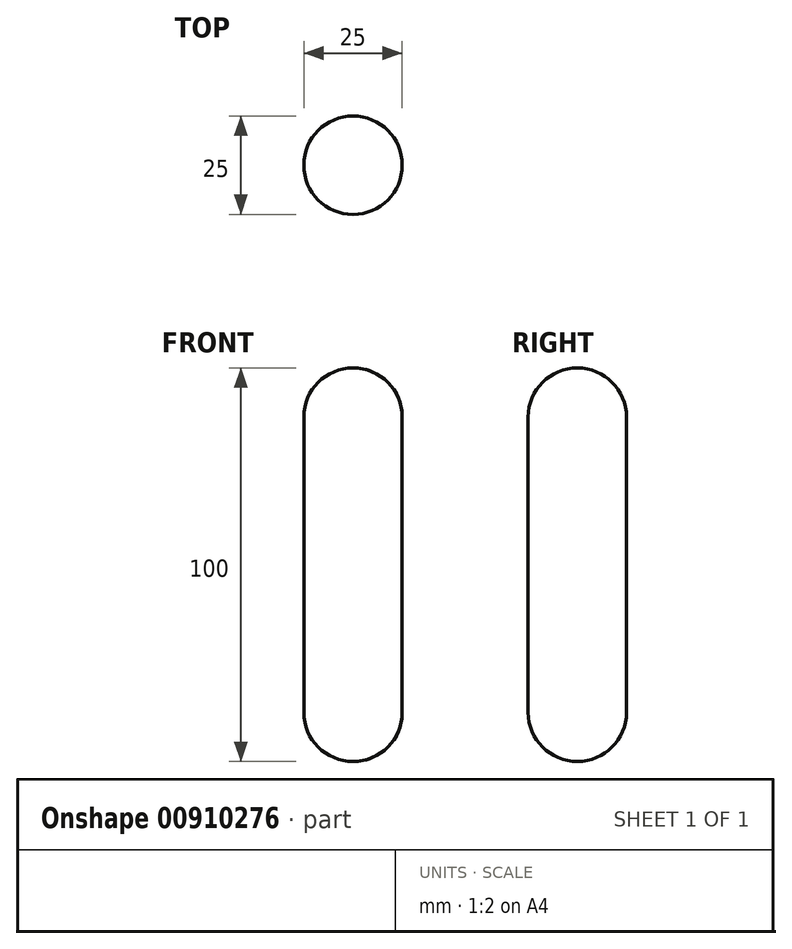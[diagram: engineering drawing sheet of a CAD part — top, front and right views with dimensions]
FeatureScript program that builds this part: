
annotation { "Feature Type Name" : "Feature", "Feature Type Description" : "" }
export const myFeature = defineFeature(function(context is Context, id is Id, definition is map)
    precondition{}
    {
        {
            var Q0;
            Q0=qCreatedBy(makeId("Top.planeOp"),FACE);
            var sketch = newSketch(context, id + "F0", { "sketchPlane" : qUnion([Q0])});
            skCircle(sketch, "E0", {"center": v(0, 0) * mm, "radius": 12.5 * mm});
            skSolve(sketch);
        }
        {
            var Q0;
            Q0=makeQuery(id+"F0.imprint","IMPRINT",FACE,{"disambiguationData":[TD([[makeQuery(id+"F0.imprint","IMPRINT",EDGE,{"derivedFrom":sQuery(id+"F0.wireOp",EDGE,"E0")}),1.0]])]});
            extrude(context, id + "F1", {"entities" : qUnion([Q0]), "depth" : 50 * mm, "offsetDistance" : 25 * mm});
        }
        {
            var Q0;
            Q0=makeQuery(id+"F1.opExtrude","CAP_EDGE",EDGE,{"disambiguationData":[OSD([sQuery(id+"F0.wireOp",EDGE,"E0")])],"isStart":false});
            fillet(context, id + "F2", {"entities" : qUnion([Q0]), "radius" : 12.5 * mm, "tangentPropagation" : true, "allowEdgeOverflow" : false});
        }
        {
            var Q0;
            Q0=makeQuery(id+"F1.opExtrude","SWEPT_BODY",BODY,{"disambiguationData":[OSD([sQuery(id+"F0.wireOp",EDGE,"E0")])]});
            var Q1;
            Q1=qCreatedBy(makeId("Top.planeOp"),FACE);
            mirror(context, id + "F3", {"operationType" : NewBodyOperationType.ADD, "entities" : qUnion([Q0]), "mirrorPlane" : qUnion([Q1])});
        }
    });
